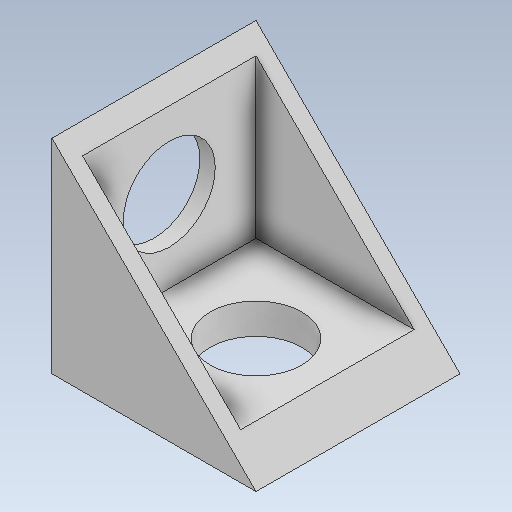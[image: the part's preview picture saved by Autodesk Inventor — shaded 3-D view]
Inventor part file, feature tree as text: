
AUTODESK INVENTOR PART (.ipt)
format: ipt  version: 2023 (Build 270158000, 158)  size: 247,296 bytes
history: native  units: in
note: dims shown in document units (in); Inventor stores cm internally (conversion verified against a paired STEP export)
features: extrude x5, sketch x5
ambient origin geometry x8: Origin, YZ Plane, XZ Plane, XY Plane, X Axis, Y Axis, Z Axis, Center Point
bodies: Solid1 (feature_tree)
feature tree (10):
  extrude  "Extrusion1"  Depth=0.7874in
  extrude  "Extrusion2"  Depth=0.6693in
  extrude  "Extrusion6"  Depth=0.6693in TaperAngle=0.0deg
  sketch  "Sketch7"  dims[d16=0.0in d17=0.0in d18=0.315in]
  extrude  "Extrusion7"  Depth=0.315in
  extrude  "Extrusion8"  Depth=0.3937in
  sketch  "Sketch1"  dims[d0=0.7874in d1=0.7874in]
  sketch  "Sketch2"  dims[d2=0.7874in d3=0.0in d4=0.6693in]
  sketch  "Sketch6"  dims[d5=0.6693in d6=0.6693in d7=0.0in]
  sketch  "Sketch8"  dims[d19=0.3543in d20=0.3543in d21=0.3937in d22=0.0in d23=0.3937in d24=0.0in]
